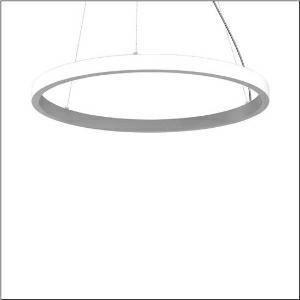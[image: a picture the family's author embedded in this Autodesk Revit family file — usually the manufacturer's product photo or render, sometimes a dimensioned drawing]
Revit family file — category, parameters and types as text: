
# Revit family: silica_21_ring-o_5pjbo4d3204a
name_source: partatom
category: Lighting Fixtures
units: mm (PartAtom-declared; Revit-internal decimal feet)

## family parameters
Cut with Voids When Loaded = No
Host = Face
Light Source = No
Part Type = Normal
Room Calculation Point = No
Round Connector Dimension = Use Diameter
Shared = No

## types (1)
- Silica 21 Ring-O (1 x LED, 9260 lm, 140 W, 4000K)
    Apparent Load = 140 VA
    CIE Flux Codes = 2 16 49 50 100
    Color Rendering = 80
    Color Temperature = 4000K
    Default Elevation = 1800 mm
    Description = Silica 21 Ring-O, suspended luminaire, of PMMA, frosted, light emission: outer ring side luminous distribution, primary light characteristic: symmetric, installation type: suspended mounting, LED, rated luminous flux: 9.260lm, luminous efficacy: 66lm/W, light colour: 840, colour temperature: 4000K, control gear: DALI 2, with terminal, 5-pole, mains connection: 230V, AC/DC, 0/50..60Hz, rated input power: 140W, housing, of extruded aluminium section, metallic grey (RAL 9006), diameter: 1.480mm, ceiling canopy, metallic grey (RAL 9006), protection rating (lamp compartment): IP40, insulation class (complete): insulation class I (protective earthing), certification: CE, impact resistance: IK02, permissible operating ambient temperature: 0..+35°C, packaging unit: 1 piece
    Height = 48 mm  [stored 0.15748 ft]
    Lamp = 1 x LED
    Lamp Light Flux = 9260 lm
    Lamp Power = 140 W
    Lamp count = 1
    Length = 1480 mm
    Luminous efficacy = 66 lm/W
    Manufacturer = Siteco
    ModVariant = No
    Model = 5PJBO4D3204A
    Mounting Place = Ceiling
    Mounting Type = Pendant
    Number of Poles = 1
    OnlyDefault = Yes
    Power Factor = 1
    Product Name = Silica 21 Ring-O
    Product group = suspended luminaire
    ProductGroupID = 904
    Protection Class = Protection class I
    Protection Degree = IP 40
    RLX_Detail_Level = 1
    RLX_Emergency_Light_Flux = 0 lm
    RLX_Emergency_Type = 0
    RLX_Emergency_Type_DB = No
    RlxData = <blob elided: 18405 chars, md5=6fdc6040>
    Socket = socket
    Standby Power = 0 W
    System Light Flux = 9260 lm
    System Power = 140 W
    Type Comments = Product without accessories
    Type Image = l_1251764.jpg
    URL = http://relux.com
    VarID = ---
    Voltage = 0 V
    Weight = 0.00 kg
    Width = 0 mm  [stored 0 ft]

note: [stored X ft] marks values corroborated as IEEE doubles in the binary element streams (Revit-internal decimal feet)

## geometry (parser evidence)
native form markers: Blend x4, Sweep x11
no freeform markers — native parametric forms only
